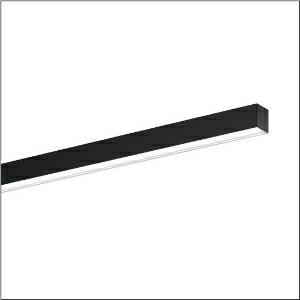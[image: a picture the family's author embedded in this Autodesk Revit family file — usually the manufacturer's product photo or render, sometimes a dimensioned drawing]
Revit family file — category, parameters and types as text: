
# Revit family: silica_21_51mx20tbt2b
name_source: partatom
category: Lighting Fixtures
units: mm (PartAtom-declared; Revit-internal decimal feet)

## family parameters
Cut with Voids When Loaded = No
Host = Face
Light Source = No
Part Type = Normal
Room Calculation Point = No
Round Connector Dimension = Use Diameter
Shared = No

## types (1)
- --- (1 x LED, 3000 lm, 25.6 W, 6500K)
    Apparent Load = 26 VA
    CIE Flux Codes = 48 79 96 100 100
    Color Rendering = 80
    Color Temperature = 6500K
    Default Elevation = 1800 mm
    Description = Silica 21, office luminaire, primary optical cover: cover, of PMMA, opal, light emission: direct distribution, primary light characteristic: symmetric, installation type: surface-mounted, LED, rated luminous flux: 3.000lm, luminous efficacy: 112lm/W, light colour: 8tw, colour temperature: 2700..6500K, control gear: DALI DT8, with terminal, 3+2-pole, max. 2.5mm², mains connection: 220..240V, AC, 50/60Hz, rated input power: 26.9W, luminaire housing, of aluminium, matt jet black (RAL 9005), length: 1.504mm, width: 53mm, height: 53mm, protection rating (complete): IP20, insulation class (complete): insulation class I (protective earthing), certification: CE, permissible operating ambient temperature: 0..+35°C, standard: EN 50419, packaging unit: 1 piece
    Height = 53 mm
    Lamp = 1 x LED
    Lamp Light Flux = 3000 lm
    Lamp Power = 25.6 W
    Lamp count = 1
    Length = 1504 mm
    Luminous efficacy = 117 lm/W
    Manufacturer = Siteco
    ModVariant = No
    Model = 51MX20TBT2B
    Mounting Place = Ceiling
    Mounting Type = Surface mounted
    Number of Poles = 1
    OnlyDefault = Yes
    Power Factor = 1
    Product Name = Silica 21
    Product group = office luminaire | ceiling mounted
    ProductGroupID = 301
    Protection Class = Protection class I
    Protection Degree = IP 20
    RLX_Detail_Level = 1
    RLX_Emergency_Light_Flux = 0 lm
    RLX_Emergency_Type = 0
    RLX_Emergency_Type_DB = No
    RlxData = <blob elided: 25637 chars, md5=df3c34f6>
    Socket = socket
    Standby Power = 0 W
    System Light Flux = 3000 lm
    System Power = 26 W
    Type Comments = individual setting
    Type Image = l_1335925.jpg
    URL = http://relux.com
    VarID = @adj_139181
    Voltage = 0 V
    Weight = 0.00 kg
    Width = 53 mm

## geometry (parser evidence)
native form markers: Blend x4, Sweep x11
no freeform markers — native parametric forms only
